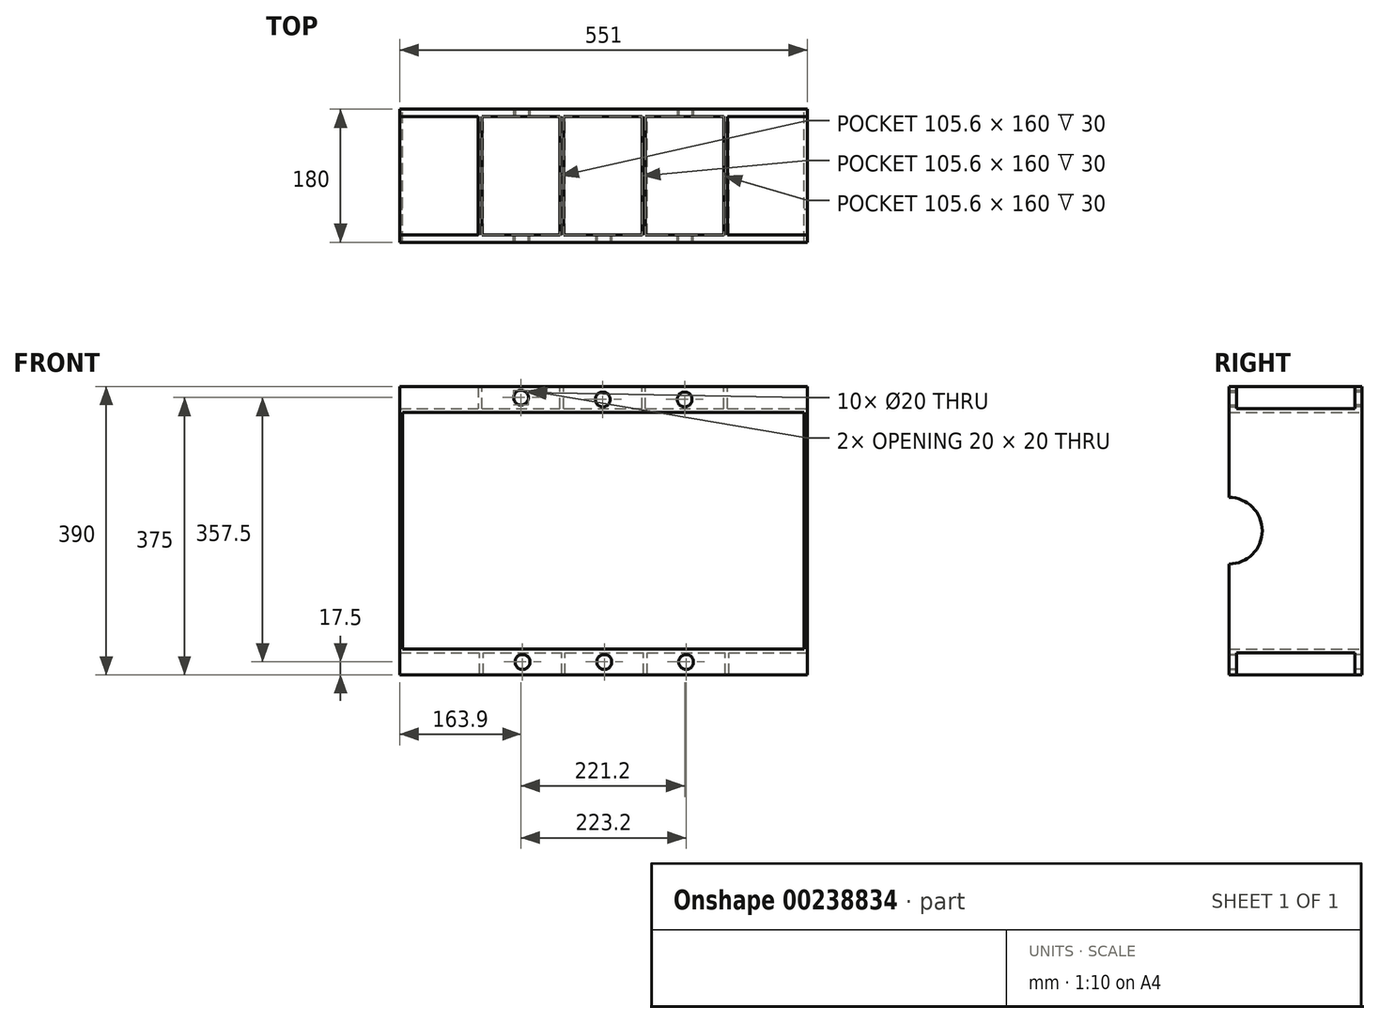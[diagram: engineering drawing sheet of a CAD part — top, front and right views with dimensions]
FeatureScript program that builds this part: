
annotation { "Feature Type Name" : "Feature", "Feature Type Description" : "" }
export const myFeature = defineFeature(function(context is Context, id is Id, definition is map)
    precondition{}
    {
        {
            var Q0;
            Q0=qCreatedBy(makeId("Front.planeOp"),FACE);
            var sketch = newSketch(context, id + "F0", { "sketchPlane" : qUnion([Q0])});
            skLineSegment(sketch, "E0.bottom", {"start": v(0, 0) * mm, "end": v(551, 0) * mm});
            skLineSegment(sketch, "E0.top", {"start": v(0, 330) * mm, "end": v(551, 330) * mm});
            skLineSegment(sketch, "E0.left", {"start": v(0, 0) * mm, "end": v(0, 330) * mm});
            skLineSegment(sketch, "E0.right", {"start": v(551, 0) * mm, "end": v(551, 330) * mm});
            skLineSegment(sketch, "E1.bottom", {"start": v(4, 5) * mm, "end": v(547, 5) * mm});
            skLineSegment(sketch, "E1.top", {"start": v(4, 325) * mm, "end": v(547, 325) * mm});
            skLineSegment(sketch, "E1.left", {"start": v(4, 5) * mm, "end": v(4, 325) * mm});
            skLineSegment(sketch, "E1.right", {"start": v(547, 5) * mm, "end": v(547, 325) * mm});
            skSolve(sketch);
        }
        {
            var Q0;
            Q0=makeQuery(id+"F0.imprint","IMPRINT",FACE,{"disambiguationData":[TD([[makeQuery(id+"F0.imprint","IMPRINT",EDGE,{"derivedFrom":sQuery(id+"F0.wireOp",EDGE,"E0.bottom")}),1.0]])]});
            extrude(context, id + "F1", {"entities" : qUnion([Q0]), "depth" : 180 * mm});
        }
        {
            var Q0;
            Q0=makeQuery(id+"F1.opExtrude","SWEPT_FACE",FACE,{"disambiguationData":[OSD([sQuery(id+"F0.wireOp",EDGE,"E0.right")])]});
            var sketch = newSketch(context, id + "F2", { "sketchPlane" : qUnion([Q0])});
            skCircle(sketch, "E2", {"center": v(-180, 165) * mm, "radius": 45 * mm});
            skSolve(sketch);
        }
        {
            var Q0;
            {var subQ0=sQuery(id+"F2.wireOp",EDGE,"E2");var subQ1=makeQuery(id+"F1.opExtrude","CAP_EDGE",EDGE,{"disambiguationData":[OSD([sQuery(id+"F0.wireOp",EDGE,"E0.right")])],"isStart":false});var subQ2=makeQuery(id+"F2.imprint","INTERSECT",VERTEX,{"disambiguationData":[OD(0.0)],"derivedFrom":[subQ1,subQ0]});Q0=makeQuery(id+"F2.imprint","IMPRINT",FACE,{"disambiguationData":[TD([[makeQuery(id+"F2.imprint","IMPRINT",EDGE,{"disambiguationData":[TD([[subQ2,1.0]])],"derivedFrom":subQ0}),1.0]])]});}
            var Q1;
            {var subQ0=sQuery(id+"F2.wireOp",EDGE,"E2");var subQ1=makeQuery(id+"F1.opExtrude","CAP_EDGE",EDGE,{"disambiguationData":[OSD([sQuery(id+"F0.wireOp",EDGE,"E0.right")])],"isStart":false});var subQ2=makeQuery(id+"F2.imprint","INTERSECT",VERTEX,{"disambiguationData":[OD(0.0)],"derivedFrom":[subQ1,subQ0]});Q1=makeQuery(id+"F2.imprint","IMPRINT",FACE,{"disambiguationData":[TD([[makeQuery(id+"F2.imprint","IMPRINT",EDGE,{"disambiguationData":[TD([[subQ2,-1.0]])],"derivedFrom":subQ0}),1.0]])]});}
            extrude(context, id + "F3", {"entities" : qUnion([Q0, Q1]), "operationType" : NewBodyOperationType.REMOVE, "endBound" : BoundingType.THROUGH_ALL, "oppositeDirection" : true, "depth" : 25 * mm});
        }
        {
            var Q0;
            Q0=makeQuery(id+"F1.opExtrude","SWEPT_FACE",FACE,{"disambiguationData":[OSD([sQuery(id+"F0.wireOp",EDGE,"E0.right")])]});
            var sketch = newSketch(context, id + "F4", { "sketchPlane" : qUnion([Q0])});
            skLineSegment(sketch, "E3.bottom", {"start": v(-180, 0) * mm, "end": v(-170, 0) * mm});
            skLineSegment(sketch, "E3.top", {"start": v(-180, -30) * mm, "end": v(-170, -30) * mm});
            skLineSegment(sketch, "E3.left", {"start": v(-180, 0) * mm, "end": v(-180, -30) * mm});
            skLineSegment(sketch, "E3.right", {"start": v(-170, 0) * mm, "end": v(-170, -30) * mm});
            skLineSegment(sketch, "E4.bottom", {"start": v(0, 0) * mm, "end": v(-10, 0) * mm});
            skLineSegment(sketch, "E4.top", {"start": v(0, -30) * mm, "end": v(-10, -30) * mm});
            skLineSegment(sketch, "E4.left", {"start": v(0, 0) * mm, "end": v(0, -30) * mm});
            skLineSegment(sketch, "E4.right", {"start": v(-10, 0) * mm, "end": v(-10, -30) * mm});
            skLineSegment(sketch, "E5.bottom", {"start": v(-180, 330) * mm, "end": v(-170, 330) * mm});
            skLineSegment(sketch, "E5.top", {"start": v(-180, 360) * mm, "end": v(-170, 360) * mm});
            skLineSegment(sketch, "E5.left", {"start": v(-180, 330) * mm, "end": v(-180, 360) * mm});
            skLineSegment(sketch, "E5.right", {"start": v(-170, 330) * mm, "end": v(-170, 360) * mm});
            skLineSegment(sketch, "E6.bottom", {"start": v(0, 330) * mm, "end": v(-10, 330) * mm});
            skLineSegment(sketch, "E6.top", {"start": v(0, 360) * mm, "end": v(-10, 360) * mm});
            skLineSegment(sketch, "E6.left", {"start": v(0, 330) * mm, "end": v(0, 360) * mm});
            skLineSegment(sketch, "E6.right", {"start": v(-10, 330) * mm, "end": v(-10, 360) * mm});
            skSolve(sketch);
        }
        {
            var Q0;
            Q0 = qSketchRegion(id + "F4", true);
            var Q1;
            Q1=makeQuery(id+"F1.opExtrude","SWEPT_FACE",FACE,{"disambiguationData":[OSD([sQuery(id+"F0.wireOp",EDGE,"E0.left")])]});
            extrude(context, id + "F5", {"entities" : qUnion([Q0]), "operationType" : NewBodyOperationType.ADD, "endBound" : BoundingType.UP_TO_SURFACE, "oppositeDirection" : true, "endBoundEntityFace" : qUnion([Q1]), "depth" : 25 * mm});
        }
        {
            var Q0;
            Q0=makeQuery(id+"F5.opExtrude","SWEPT_FACE",FACE,{"disambiguationData":[OSD([sQuery(id+"F4.wireOp",EDGE,"E4.right")])]});
            var sketch = newSketch(context, id + "F6", { "sketchPlane" : qUnion([Q0])});
            skLineSegment(sketch, "E7.bottom", {"start": v(108.1, -30) * mm, "end": v(113.1, -30) * mm});
            skLineSegment(sketch, "E7.top", {"start": v(108.1, 0) * mm, "end": v(113.1, 0) * mm});
            skLineSegment(sketch, "E7.left", {"start": v(108.1, -30) * mm, "end": v(108.1, 0) * mm});
            skLineSegment(sketch, "E7.right", {"start": v(113.1, -30) * mm, "end": v(113.1, 0) * mm});
            skLineSegment(sketch, "E8.bottom", {"start": v(218.7, -30) * mm, "end": v(223.7, -30) * mm});
            skLineSegment(sketch, "E8.top", {"start": v(218.7, 0) * mm, "end": v(223.7, 0) * mm});
            skLineSegment(sketch, "E8.left", {"start": v(218.7, -30) * mm, "end": v(218.7, 0) * mm});
            skLineSegment(sketch, "E8.right", {"start": v(223.7, -30) * mm, "end": v(223.7, 0) * mm});
            skLineSegment(sketch, "E9.bottom", {"start": v(329.3, -30) * mm, "end": v(334.3, -30) * mm});
            skLineSegment(sketch, "E9.top", {"start": v(329.3, 0) * mm, "end": v(334.3, 0) * mm});
            skLineSegment(sketch, "E9.left", {"start": v(329.3, -30) * mm, "end": v(329.3, 0) * mm});
            skLineSegment(sketch, "E9.right", {"start": v(334.3, -30) * mm, "end": v(334.3, 0) * mm});
            skLineSegment(sketch, "E10.bottom", {"start": v(439.9, -30) * mm, "end": v(444.9, -30) * mm});
            skLineSegment(sketch, "E10.top", {"start": v(439.9, 0) * mm, "end": v(444.9, 0) * mm});
            skLineSegment(sketch, "E10.left", {"start": v(439.9, -30) * mm, "end": v(439.9, 0) * mm});
            skLineSegment(sketch, "E10.right", {"start": v(444.9, -30) * mm, "end": v(444.9, 0) * mm});
            skSolve(sketch);
        }
        {
            var Q0;
            Q0 = qSketchRegion(id + "F6", true);
            extrude(context, id + "F7", {"entities" : qUnion([Q0]), "operationType" : NewBodyOperationType.ADD, "endBound" : BoundingType.UP_TO_NEXT, "depth" : 25 * mm});
        }
        {
            var Q0;
            Q0=makeQuery(id+"F5.opExtrude","SWEPT_FACE",FACE,{"disambiguationData":[OSD([sQuery(id+"F4.wireOp",EDGE,"E6.right")])]});
            var sketch = newSketch(context, id + "F8", { "sketchPlane" : qUnion([Q0])});
            skLineSegment(sketch, "E11.bottom", {"start": v(442.9, 360) * mm, "end": v(437.9, 360) * mm});
            skLineSegment(sketch, "E11.top", {"start": v(442.9, 330) * mm, "end": v(437.9, 330) * mm});
            skLineSegment(sketch, "E11.left", {"start": v(442.9, 360) * mm, "end": v(442.9, 330) * mm});
            skLineSegment(sketch, "E11.right", {"start": v(437.9, 360) * mm, "end": v(437.9, 330) * mm});
            skLineSegment(sketch, "E12.bottom", {"start": v(332.3, 360) * mm, "end": v(327.3, 360) * mm});
            skLineSegment(sketch, "E12.top", {"start": v(332.3, 330) * mm, "end": v(327.3, 330) * mm});
            skLineSegment(sketch, "E12.left", {"start": v(332.3, 360) * mm, "end": v(332.3, 330) * mm});
            skLineSegment(sketch, "E12.right", {"start": v(327.3, 360) * mm, "end": v(327.3, 330) * mm});
            skLineSegment(sketch, "E13.bottom", {"start": v(221.7, 360) * mm, "end": v(216.7, 360) * mm});
            skLineSegment(sketch, "E13.top", {"start": v(221.7, 330) * mm, "end": v(216.7, 330) * mm});
            skLineSegment(sketch, "E13.left", {"start": v(216.7, 360) * mm, "end": v(216.7, 330) * mm});
            skLineSegment(sketch, "E13.right", {"start": v(221.7, 360) * mm, "end": v(221.7, 330) * mm});
            skLineSegment(sketch, "E14.bottom", {"start": v(111.1, 360) * mm, "end": v(106.1, 360) * mm});
            skLineSegment(sketch, "E14.top", {"start": v(111.1, 330) * mm, "end": v(106.1, 330) * mm});
            skLineSegment(sketch, "E14.left", {"start": v(106.1, 360) * mm, "end": v(106.1, 330) * mm});
            skLineSegment(sketch, "E14.right", {"start": v(111.1, 360) * mm, "end": v(111.1, 330) * mm});
            skSolve(sketch);
        }
        {
            var Q0;
            Q0 = qSketchRegion(id + "F8", true);
            extrude(context, id + "F9", {"entities" : qUnion([Q0]), "operationType" : NewBodyOperationType.ADD, "endBound" : BoundingType.UP_TO_NEXT, "depth" : 25 * mm});
        }
        {
            var Q0;
            Q0=makeQuery(id+"F9.boolean.opBoolean","SPLIT",FACE,{"disambiguationData":[TD([makeQuery(id+"F9.opExtrude","SWEPT_FACE",FACE,{"disambiguationData":[OSD([sQuery(id+"F8.wireOp",EDGE,"E13.left")])]})])],"derivedFrom":makeQuery(id+"F5.opExtrude","SWEPT_FACE",FACE,{"disambiguationData":[OSD([sQuery(id+"F4.wireOp",EDGE,"E5.right")])]})});
            var sketch = newSketch(context, id + "F10", { "sketchPlane" : qUnion([Q0])});
            skCircle(sketch, "E15", {"center": v(-163.9, 345) * mm, "radius": 10 * mm});
            skPoint(sketch, "E15.centerSnap0", {"position": v(-163.9, 360) * mm});
            skPoint(sketch, "E15.centerSnap1", {"position": v(-216.7, 345) * mm});
            skCircle(sketch, "E16", {"center": v(-385.1, 342.5) * mm, "radius": 10 * mm});
            skCircle(sketch, "E17", {"center": v(-387.1, -12.5) * mm, "radius": 10 * mm});
            skCircle(sketch, "E18", {"center": v(-165.96, -12.5) * mm, "radius": 10 * mm});
            skSolve(sketch);
        }
        {
            var Q0;
            Q0=makeQuery(id+"F10.imprint","IMPRINT",FACE,{"disambiguationData":[TD([[makeQuery(id+"F10.imprint","IMPRINT",EDGE,{"derivedFrom":sQuery(id+"F10.wireOp",EDGE,"E18")}),1.0]])]});
            var Q1;
            Q1=makeQuery(id+"F10.imprint","IMPRINT",FACE,{"disambiguationData":[TD([[makeQuery(id+"F10.imprint","IMPRINT",EDGE,{"derivedFrom":sQuery(id+"F10.wireOp",EDGE,"E17")}),1.0]])]});
            var Q2;
            Q2=makeQuery(id+"F10.imprint","IMPRINT",FACE,{"disambiguationData":[TD([[makeQuery(id+"F10.imprint","IMPRINT",EDGE,{"derivedFrom":sQuery(id+"F10.wireOp",EDGE,"E15")}),1.0]])]});
            var Q3;
            Q3=makeQuery(id+"F10.imprint","IMPRINT",FACE,{"disambiguationData":[TD([[makeQuery(id+"F10.imprint","IMPRINT",EDGE,{"derivedFrom":sQuery(id+"F10.wireOp",EDGE,"E16")}),1.0]])]});
            extrude(context, id + "F11", {"entities" : qUnion([Q0, Q1, Q2, Q3]), "operationType" : NewBodyOperationType.REMOVE, "oppositeDirection" : true, "depth" : 25 * mm});
        }
        {
            var Q0;
            Q0=makeQuery(id+"F10.imprint","IMPRINT",FACE,{"disambiguationData":[TD([[makeQuery(id+"F10.imprint","IMPRINT",EDGE,{"derivedFrom":sQuery(id+"F10.wireOp",EDGE,"E15")}),1.0]])]});
            var Q1;
            Q1=makeQuery(id+"F10.imprint","IMPRINT",FACE,{"disambiguationData":[TD([[makeQuery(id+"F10.imprint","IMPRINT",EDGE,{"derivedFrom":sQuery(id+"F10.wireOp",EDGE,"E16")}),1.0]])]});
            var Q2;
            Q2=makeQuery(id+"F10.imprint","IMPRINT",FACE,{"disambiguationData":[TD([[makeQuery(id+"F10.imprint","IMPRINT",EDGE,{"derivedFrom":sQuery(id+"F10.wireOp",EDGE,"E18")}),1.0]])]});
            var Q3;
            Q3=makeQuery(id+"F10.imprint","IMPRINT",FACE,{"disambiguationData":[TD([[makeQuery(id+"F10.imprint","IMPRINT",EDGE,{"derivedFrom":sQuery(id+"F10.wireOp",EDGE,"E17")}),1.0]])]});
            extrude(context, id + "F12", {"entities" : qUnion([Q0, Q1, Q2, Q3]), "operationType" : NewBodyOperationType.REMOVE, "endBound" : BoundingType.THROUGH_ALL, "depth" : 25 * mm});
        }
        {
            var Q0;
            {var subQ0=sQuery(id+"F0.wireOp",EDGE,"E1.bottom");var subQ1=sQuery(id+"F0.wireOp",EDGE,"E0.left");var subQ2=sQuery(id+"F0.wireOp",EDGE,"E0.right");var subQ3=sQuery(id+"F0.wireOp",EDGE,"E0.bottom");var subQ4=sQuery(id+"F0.wireOp",EDGE,"E1.left");var subQ5=sQuery(id+"F0.wireOp",EDGE,"E1.right");Q0=makeQuery(id+"F5.boolean.opBoolean","MERGE",FACE,{"derivedFrom":[makeQuery(id+"F3.boolean.opBoolean","SPLIT",FACE,{"disambiguationData":[TD([makeQuery(id+"F1.opExtrude","SWEPT_FACE",FACE,{"disambiguationData":[OSD([subQ3])]})])],"derivedFrom":makeQuery(id+"F1.opExtrude","CAP_FACE",FACE,{"disambiguationData":[OSD([subQ3,sQuery(id+"F0.wireOp",EDGE,"E0.top"),subQ1,subQ2,subQ0,sQuery(id+"F0.wireOp",EDGE,"E1.top"),subQ4,subQ5])],"isStart":false})}),makeQuery(id+"F5.opExtrude","SWEPT_FACE",FACE,{"disambiguationData":[OSD([sQuery(id+"F4.wireOp",EDGE,"E3.left")])]})]});}
            var sketch = newSketch(context, id + "F13", { "sketchPlane" : qUnion([Q0])});
            skCircle(sketch, "E19", {"center": v(276.5, -12.5) * mm, "radius": 10 * mm});
            skCircle(sketch, "E20", {"center": v(274.5, 342.5) * mm, "radius": 10 * mm});
            skSolve(sketch);
        }
        {
            var Q0;
            Q0=makeQuery(id+"F13.imprint","IMPRINT",FACE,{"disambiguationData":[TD([[makeQuery(id+"F13.imprint","IMPRINT",EDGE,{"derivedFrom":sQuery(id+"F13.wireOp",EDGE,"E20")}),1.0]])]});
            var Q1;
            Q1=makeQuery(id+"F13.imprint","IMPRINT",FACE,{"disambiguationData":[TD([[makeQuery(id+"F13.imprint","IMPRINT",EDGE,{"derivedFrom":sQuery(id+"F13.wireOp",EDGE,"E19")}),1.0]])]});
            extrude(context, id + "F14", {"entities" : qUnion([Q0, Q1]), "operationType" : NewBodyOperationType.REMOVE, "oppositeDirection" : true, "depth" : 25 * mm});
        }
    });
